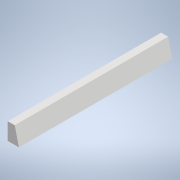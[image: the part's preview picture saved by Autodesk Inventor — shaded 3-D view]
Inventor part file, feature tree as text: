
AUTODESK INVENTOR PART (.ipt)
format: ipt  version: 2020 (Build 240168000, 168)  size: 95,232 bytes
history: native  units: in
note: dims shown in document units (in); Inventor stores cm internally (conversion verified against a paired STEP export)
features: other x7, reference x5, sketch x1, plane x1, extrude x1
ambient origin geometry x8: Origin, YZ Plane, XZ Plane, XY Plane, X Axis, Y Axis, Z Axis, Center Point
bodies: Solid1 (feature_tree)
feature tree (15):
  sketch  "Sketch1"  dims[d0=1.0in d1=0.0in]
  plane  "Work Plane1"
  extrude  "Extrusion1"  [1 undecoded]
  reference  "Reference1"
  reference  "Reference2"
  reference  "Reference3"
  reference  "Reference4"
  reference  "Reference5"
  other  "<userpath>\Documents\FRC\2020\Prototype1.iam"
  other  "Prototype1.iam"
  other  "DriveBase2020:1"
  other  "AM14U3 Long Half:2"
  other  "AM14U3 Long Frame Half_3"
  other  "AM14U3 Outside Sheet Rev1_DefaultSM-FLAT-PATTERN_137"
  other  "AM14U3 End Sheet Square:2"
note: 1 required parameter value undecoded (feature->parameter linkage not recoverable at this tier; creation-order binding heuristic only, values carry confidence <= 0.55)
